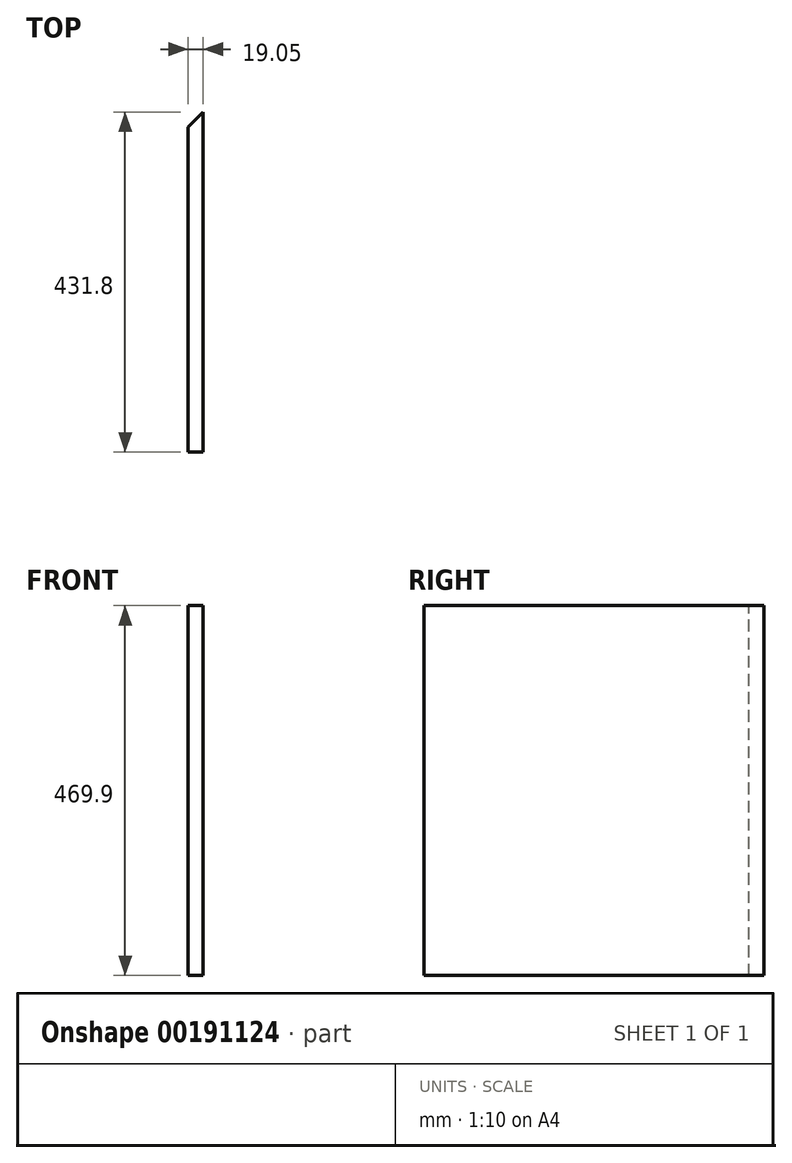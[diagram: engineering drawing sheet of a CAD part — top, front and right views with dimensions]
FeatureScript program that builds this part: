
annotation { "Feature Type Name" : "Feature", "Feature Type Description" : "" }
export const myFeature = defineFeature(function(context is Context, id is Id, definition is map)
    precondition{}
    {
        {
            var Q0;
            Q0=qCreatedBy(makeId("Right.planeOp"),FACE);
            var sketch = newSketch(context, id + "F0", { "sketchPlane" : qUnion([Q0])});
            skLineSegment(sketch, "E0.bottom", {"start": v(215.9, 234.95) * mm, "end": v(-215.9, 234.95) * mm});
            skLineSegment(sketch, "E0.top", {"start": v(215.9, -234.95) * mm, "end": v(-215.9, -234.95) * mm});
            skLineSegment(sketch, "E0.left", {"start": v(215.9, 234.95) * mm, "end": v(215.9, -234.95) * mm});
            skLineSegment(sketch, "E0.right", {"start": v(-215.9, 234.95) * mm, "end": v(-215.9, -234.95) * mm});
            skPoint(sketch, "E0.middle", {"position": v(0, 0) * mm});
            skSolve(sketch);
        }
        {
            var Q0;
            Q0 = qSketchRegion(id + "F0", true);
            extrude(context, id + "F1", {"entities" : qUnion([Q0]), "depth" : 19.05 * mm});
        }
        {
            var Q0;
            Q0=makeQuery(id+"F1.opExtrude","SWEPT_FACE",FACE,{"disambiguationData":[OSD([sQuery(id+"F0.wireOp",EDGE,"E0.bottom")])]});
            var sketch = newSketch(context, id + "F2", { "sketchPlane" : qUnion([Q0])});
            skLineSegment(sketch, "E1", {"start": v(19.05, 215.9) * mm, "end": v(0, 196.85) * mm});
            skLineSegment(sketch, "E2", {"start": v(0, 196.85) * mm, "end": v(0, 215.9) * mm});
            skLineSegment(sketch, "E3", {"start": v(0, 215.9) * mm, "end": v(19.05, 215.9) * mm});
            skSolve(sketch);
        }
        {
            var Q0;
            Q0 = qSketchRegion(id + "F2", true);
            extrude(context, id + "F3", {"entities" : qUnion([Q0]), "operationType" : NewBodyOperationType.REMOVE, "endBound" : BoundingType.THROUGH_ALL, "oppositeDirection" : true, "depth" : 25.4 * mm});
        }
    });
